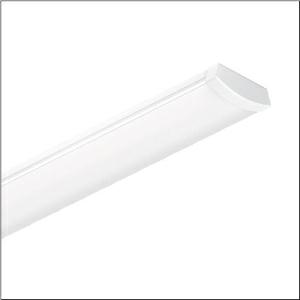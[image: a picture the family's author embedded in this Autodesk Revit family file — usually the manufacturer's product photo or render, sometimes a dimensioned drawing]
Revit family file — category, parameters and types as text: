
# Revit family: siluette_r__21_51ln12mnm70a_66ce
name_source: partatom
category: Lighting Fixtures
units: mm (PartAtom-declared; Revit-internal decimal feet)

## family parameters
Cut with Voids When Loaded = No
Host = Face
Light Source = No
Part Type = Normal
Room Calculation Point = No
Round Connector Dimension = Use Diameter
Shared = No

## types (1)
- --- (1 x LED, 4320 lm, 28.8 W, 5000K)
    Apparent Load = 29 VA
    CIE Flux Codes = 43 73 92 94 100
    Color Rendering = 80
    Color Temperature = 5000K
    Default Elevation = 1800 mm
    Description = Siluette® 21, office luminaire, primary optical cover: enclosure, of PC, frosted, light emission: direct distribution, primary light characteristic: symmetric, installation type: suspended mounting, surface-mounted, LED, rated luminous flux: 7.000lm, luminous efficacy: 140lm/W, light colour: 830/840/850, colour temperature: 3000/4000/5000K, with terminal, 3-pole, mains connection: 220..240V, AC, 50/60Hz, rated input power: 50W, housing, of sheet steel, white, length: 1.500mm, width: 152mm, height: 53mm, end cap, of PMMA, white, protection rating (complete): IP44, insulation class (complete): insulation class I (protective earthing), certification: CE, UKCA, protection symbol: D, permissible operating ambient temperature: -20..+40°C, contact your sales advisor before using the luminaires in applications with unclear chemical exposure, large temperature fluctuations or condensation-forming humidity, corresponds to IFS (International Featured Standards) requirements for safety and quality in the food industry, packaging unit: 1 piece
    Height = 52 mm  [stored 0.170604 ft]
    Lamp = 1 x LED
    Lamp Light Flux = 4320 lm
    Lamp Power = 28.8 W
    Lamp count = 1
    Length = 1485 mm
    Luminous efficacy = 150 lm/W
    Manufacturer = Siteco
    ModVariant = No
    Model = 51LN12MNM70A
    Mounting Place = Ceiling
    Mounting Type = Pendant
    Number of Poles = 1
    OnlyDefault = Yes
    Power Factor = 1
    Product Name = Siluette® 21
    Product group = office luminaire | ceiling pendant
    ProductGroupID = 902
    Protection Class = Protection class I
    Protection Degree = IP 44
    RLX_Detail_Level = 1
    RLX_Emergency_Light_Flux = 0 lm
    RLX_Emergency_Type = 0
    RLX_Emergency_Type_DB = No
    RlxData = <blob elided: 20177 chars, md5=ab0cd1d9>
    Socket = socket
    Standby Power = 0 W
    System Light Flux = 4320 lm
    System Power = 29 W
    Type Comments = individual setting: colour temperature 5000K, luminous flux: 61 % | (OFF | OFF | ON) | 200 mA
    Type Image = l_1296910.jpg
    URL = http://relux.com
    VarID = @adj_001809
    Voltage = 0 V
    Weight = 0.00 kg
    Width = 152 mm

note: [stored X ft] marks values corroborated as IEEE doubles in the binary element streams (Revit-internal decimal feet)

## geometry (parser evidence)
native form markers: Blend x4, Sweep x12
no freeform markers — native parametric forms only
